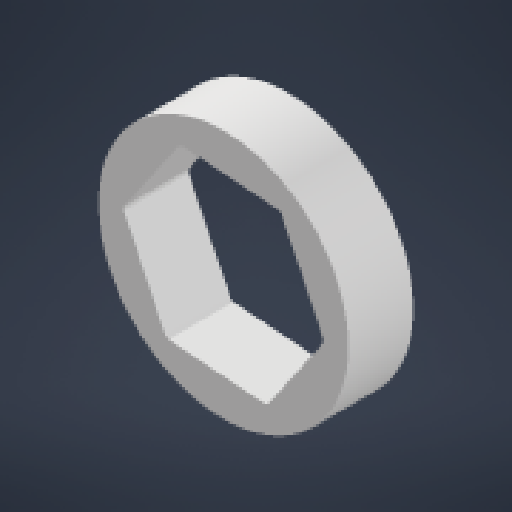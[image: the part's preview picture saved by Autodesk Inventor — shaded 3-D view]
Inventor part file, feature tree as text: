
AUTODESK INVENTOR PART (.ipt)
format: ipt  version: 2024.2 (Build 282272000, 272)  size: 136,704 bytes
history: native  units: in
note: dims shown in document units (in); Inventor stores cm internally (conversion verified against a paired STEP export)
features: sketch x1, plane x1, extrude x1
ambient origin geometry x8: Origin, YZ Plane, XZ Plane, XY Plane, X Axis, Y Axis, Z Axis, Center Point
bodies: Solid1 (feature_tree)
feature tree (3):
  sketch  "Sketch1"  dims[d0=0.3937in d1=1.0in d2=0.0in]
  plane  "Work Plane1"
  extrude  "Extrusion1"  Depth=0.3937in TaperAngle=0.0deg
